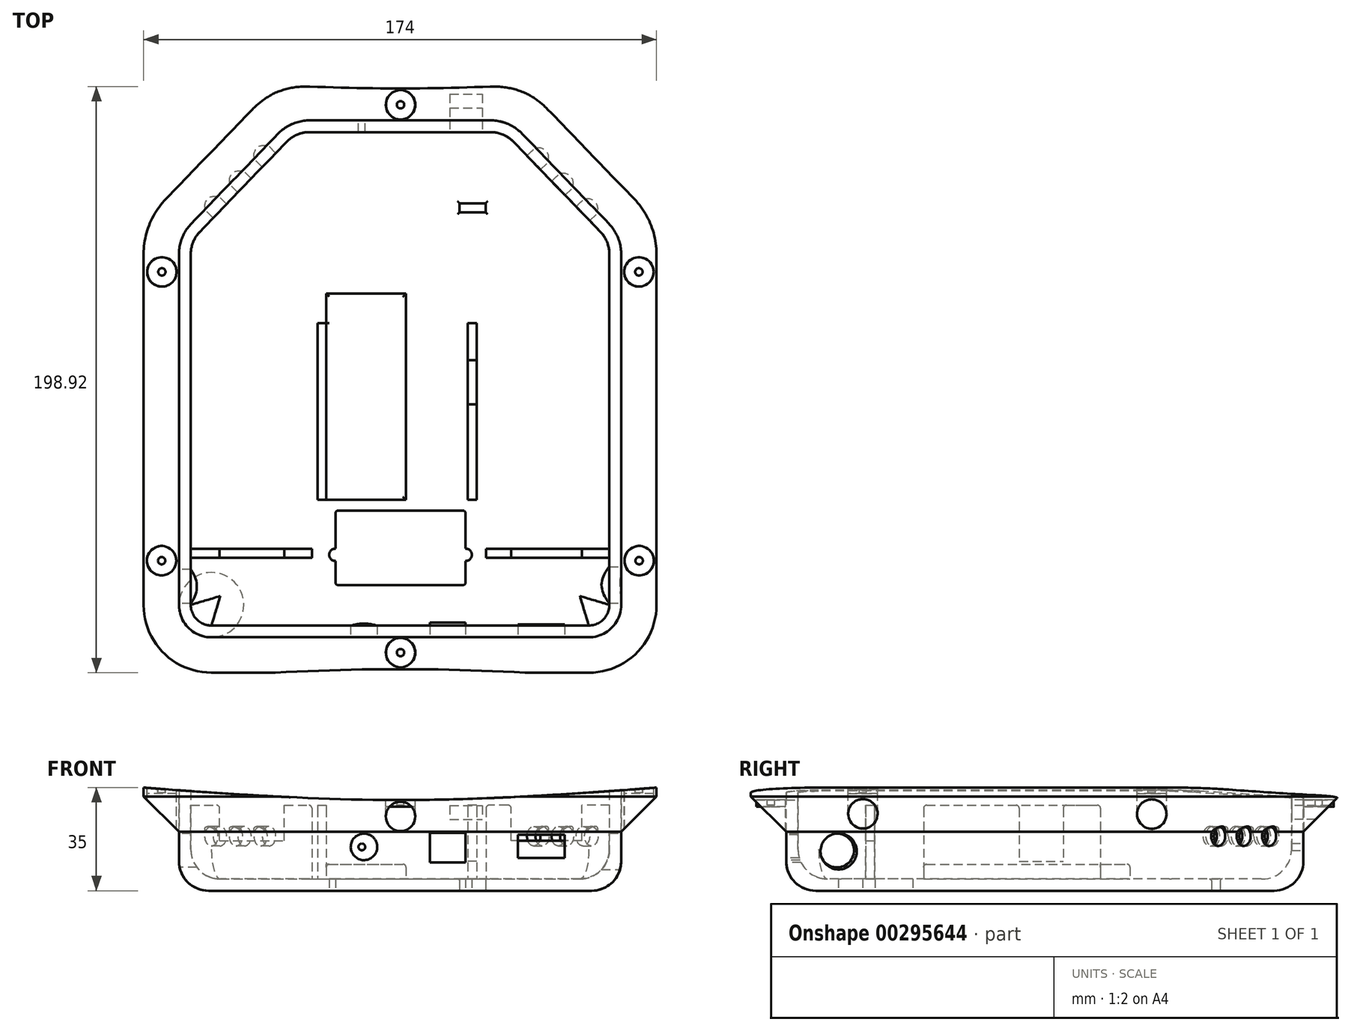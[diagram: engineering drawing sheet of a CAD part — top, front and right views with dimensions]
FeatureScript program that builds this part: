
annotation { "Feature Type Name" : "Feature", "Feature Type Description" : "" }
export const myFeature = defineFeature(function(context is Context, id is Id, definition is map)
    precondition{}
    {
        {
            var Q0;
            Q0=qCreatedBy(makeId("Top.planeOp"),FACE);
            var sketch = newSketch(context, id + "F0", { "sketchPlane" : qUnion([Q0])});
            skLineSegment(sketch, "E0.top", {"start": v(-64.15, -84.77) * mm, "end": v(63.85, -84.77) * mm});
            skLineSegment(sketch, "E0.left", {"start": v(-75.15, 45.23) * mm, "end": v(-75.15, -73.77) * mm});
            skLineSegment(sketch, "E0.right", {"start": v(74.85, 45.23) * mm, "end": v(74.85, -73.77) * mm});
            skLineSegment(sketch, "E1", {"start": v(-41.58, 86.08) * mm, "end": v(-70.95, 55.65) * mm});
            skLineSegment(sketch, "E2", {"start": v(41.27, 86.08) * mm, "end": v(70.64, 55.65) * mm});
            skLineSegment(sketch, "E3", {"start": v(-30.78, 90.67) * mm, "end": v(30.48, 90.67) * mm});
            skPoint(sketch, "E4.visualSharp", {"position": v(-37.15, 90.67) * mm});
            skArc(sketch, "E4.filletArc", {"start": v(-30.78, 90.67) * mm, "mid": v(-36.65, 89.47) * mm, "end": v(-41.58, 86.08) * mm});
            skPoint(sketch, "E5.newPointA", {"position": v(-76.04, 50.37) * mm});
            skArc(sketch, "E5.filletArc", {"start": v(-70.95, 55.65) * mm, "mid": v(-74.06, 50.85) * mm, "end": v(-75.15, 45.23) * mm});
            skPoint(sketch, "E6.newPointA", {"position": v(75.73, 50.37) * mm});
            skArc(sketch, "E6.filletArc", {"start": v(74.85, 45.23) * mm, "mid": v(73.75, 50.85) * mm, "end": v(70.64, 55.65) * mm});
            skPoint(sketch, "E7.visualSharp", {"position": v(36.85, 90.67) * mm});
            skArc(sketch, "E7.filletArc", {"start": v(41.27, 86.08) * mm, "mid": v(36.34, 89.47) * mm, "end": v(30.48, 90.67) * mm});
            skPoint(sketch, "E8.visualSharp", {"position": v(74.85, -84.77) * mm});
            skArc(sketch, "E8.filletArc", {"start": v(63.85, -84.77) * mm, "mid": v(71.62, -81.55) * mm, "end": v(74.85, -73.77) * mm});
            skPoint(sketch, "E9.visualSharp", {"position": v(-75.15, -84.77) * mm});
            skArc(sketch, "E9.filletArc", {"start": v(-75.15, -73.77) * mm, "mid": v(-71.93, -81.55) * mm, "end": v(-64.15, -84.77) * mm});
            skSolve(sketch);
        }
        {
            var Q0;
            Q0=qSketchRegion(id+"F0",true);
            extrude(context, id + "F1", {"entities" : qUnion([Q0]), "depth" : 35 * mm, "offsetDistance" : 25 * mm});
        }
        {
            var Q0;
            Q0=makeQuery(id+"F1.opExtrude","CAP_FACE",FACE,{"disambiguationData":[OSD([sQuery(id+"F0.wireOp",EDGE,"E0.bottom"),sQuery(id+"F0.wireOp",EDGE,"E0.top"),sQuery(id+"F0.wireOp",EDGE,"E0.left"),sQuery(id+"F0.wireOp",EDGE,"E0.right")])],"isStart":false});
            shell(context, id + "F2", {"entities" : qUnion([Q0]), "thickness" : 4 * mm});
        }
        {
            var Q0;
            {var subQ0=sQuery(id+"F0.wireOp",EDGE,"E0.left");Q0=makeQuery(id+"F2.opShell","OFFSET_EDGE",EDGE,{"disambiguationData":[OSD([subQ0]),TDD([makeQuery(id+"F1.opExtrude","CAP_EDGE",EDGE,{"disambiguationData":[OSD([subQ0])],"isStart":true})])]});}
            var Q1;
            {var subQ0=sQuery(id+"F0.wireOp",EDGE,"E0.right");Q1=makeQuery(id+"F2.opShell","OFFSET_EDGE",EDGE,{"disambiguationData":[OSD([subQ0]),TDD([makeQuery(id+"F1.opExtrude","CAP_EDGE",EDGE,{"disambiguationData":[OSD([subQ0])],"isStart":true})])]});}
            var Q2;
            {var subQ0=sQuery(id+"F0.wireOp",EDGE,"E0.bottom");Q2=makeQuery(id+"F2.opShell","OFFSET_EDGE",EDGE,{"disambiguationData":[OSD([subQ0]),TDD([makeQuery(id+"F1.opExtrude","CAP_EDGE",EDGE,{"disambiguationData":[OSD([subQ0])],"isStart":true})])]});}
            var Q3;
            {var subQ0=sQuery(id+"F0.wireOp",EDGE,"eb44f88f-92e2-455c-a940-064eeaeaa6cd.filletArc");Q3=makeQuery(id+"F2.opShell","OFFSET_EDGE",EDGE,{"disambiguationData":[OSD([subQ0]),TDD([makeQuery(id+"F1.opExtrude","CAP_EDGE",EDGE,{"disambiguationData":[OSD([subQ0])],"isStart":true})])]});}
            var Q4;
            {var subQ0=sQuery(id+"F0.wireOp",EDGE,"d43988df-4d56-44c7-8095-11d52762e103.filletArc");Q4=makeQuery(id+"F2.opShell","OFFSET_EDGE",EDGE,{"disambiguationData":[OSD([subQ0]),TDD([makeQuery(id+"F1.opExtrude","CAP_EDGE",EDGE,{"disambiguationData":[OSD([subQ0])],"isStart":true})])]});}
            fillet(context, id + "F3", {"entities" : qUnion([Q0, Q1, Q2, Q3, Q4]), "radius" : 10 * mm, "tangentPropagation" : true, "allowEdgeOverflow" : false});
        }
        {
            var Q0;
            Q0=makeQuery(id+"F1.opExtrude","CAP_EDGE",EDGE,{"disambiguationData":[OSD([sQuery(id+"F0.wireOp",EDGE,"E0.right")])],"isStart":true});
            var Q1;
            Q1=makeQuery(id+"F1.opExtrude","CAP_EDGE",EDGE,{"disambiguationData":[OSD([sQuery(id+"F0.wireOp",EDGE,"d43988df-4d56-44c7-8095-11d52762e103.filletArc")])],"isStart":true});
            var Q2;
            Q2=makeQuery(id+"F1.opExtrude","CAP_EDGE",EDGE,{"disambiguationData":[OSD([sQuery(id+"F0.wireOp",EDGE,"E0.bottom")])],"isStart":true});
            var Q3;
            Q3=makeQuery(id+"F1.opExtrude","CAP_EDGE",EDGE,{"disambiguationData":[OSD([sQuery(id+"F0.wireOp",EDGE,"E0.left")])],"isStart":true});
            var Q4;
            Q4=makeQuery(id+"F1.opExtrude","CAP_EDGE",EDGE,{"disambiguationData":[OSD([sQuery(id+"F0.wireOp",EDGE,"eb44f88f-92e2-455c-a940-064eeaeaa6cd.filletArc")])],"isStart":true});
            fillet(context, id + "F4", {"entities" : qUnion([Q0, Q1, Q2, Q3, Q4]), "radius" : 10 * mm, "tangentPropagation" : true, "allowEdgeOverflow" : false});
        }
        {
            var Q0;
            Q0=makeQuery(id+"FrwUbtnxUC9HyyJ_1.boolean.opBoolean","MERGE",FACE,{"derivedFrom":[makeQuery(id+"F1.opExtrude","CAP_FACE",FACE,{"disambiguationData":[OSD([sQuery(id+"F0.wireOp",EDGE,"E0.bottom"),sQuery(id+"F0.wireOp",EDGE,"E0.top"),sQuery(id+"F0.wireOp",EDGE,"E0.left"),sQuery(id+"F0.wireOp",EDGE,"E0.right"),sQuery(id+"F0.wireOp",EDGE,"eb44f88f-92e2-455c-a940-064eeaeaa6cd.filletArc"),sQuery(id+"F0.wireOp",EDGE,"d43988df-4d56-44c7-8095-11d52762e103.filletArc")])],"isStart":false}),makeQuery(id+"FrwUbtnxUC9HyyJ_1.opExtrude","CAP_FACE",FACE,{"disambiguationData":[OSD([sQuery(id+"FibHU4dr98Ndzw2_1.wireOp",EDGE,"9rjzK8EU-co4c-AKP1-GJnL-XDDrkJgZbtAS.bottom"),sQuery(id+"FibHU4dr98Ndzw2_1.wireOp",EDGE,"9rjzK8EU-co4c-AKP1-GJnL-XDDrkJgZbtAS.top"),sQuery(id+"FibHU4dr98Ndzw2_1.wireOp",EDGE,"9rjzK8EU-co4c-AKP1-GJnL-XDDrkJgZbtAS.left"),sQuery(id+"FibHU4dr98Ndzw2_1.wireOp",EDGE,"9rjzK8EU-co4c-AKP1-GJnL-XDDrkJgZbtAS.right")])],"isStart":true})]});
            var sketch = newSketch(context, id + "F5", { "sketchPlane" : qUnion([Q0])});
            skLineSegment(sketch, "E10", {"start": v(-30.78, 90.67) * mm, "end": v(30.48, 90.67) * mm});
            skLineSegment(sketch, "E11", {"start": v(74.85, 45.23) * mm, "end": v(74.85, -73.77) * mm});
            skLineSegment(sketch, "E12", {"start": v(-64.15, -84.77) * mm, "end": v(63.85, -84.77) * mm});
            skLineSegment(sketch, "E13", {"start": v(-75.15, -73.77) * mm, "end": v(-75.15, 45.23) * mm});
            skLineSegment(sketch, "E14", {"start": v(-41.58, 86.08) * mm, "end": v(-70.95, 55.65) * mm});
            skLineSegment(sketch, "E15", {"start": v(41.27, 86.08) * mm, "end": v(70.64, 55.65) * mm});
            skPoint(sketch, "E16.newPointB", {"position": v(-45.04, 90.67) * mm});
            skArc(sketch, "E16.filletArc", {"start": v(-30.78, 90.67) * mm, "mid": v(-36.65, 89.47) * mm, "end": v(-41.58, 86.08) * mm});
            skArc(sketch, "E17.filletArc", {"start": v(41.27, 86.08) * mm, "mid": v(36.34, 89.47) * mm, "end": v(30.48, 90.67) * mm});
            skPoint(sketch, "E18.newPointA", {"position": v(74.85, 61.4) * mm});
            skArc(sketch, "E18.filletArc", {"start": v(74.85, 45.23) * mm, "mid": v(73.75, 50.85) * mm, "end": v(70.64, 55.65) * mm});
            skArc(sketch, "E19.filletArc", {"start": v(-70.95, 55.65) * mm, "mid": v(-74.06, 50.85) * mm, "end": v(-75.15, 45.23) * mm});
            skPoint(sketch, "E20.newPointA", {"position": v(-75.15, -93.2) * mm});
            skPoint(sketch, "E20.newPointB", {"position": v(-86.24, -84.77) * mm});
            skArc(sketch, "E20.filletArc", {"start": v(-75.15, -73.77) * mm, "mid": v(-71.93, -81.55) * mm, "end": v(-64.15, -84.77) * mm});
            skArc(sketch, "E21.filletArc", {"start": v(63.85, -84.77) * mm, "mid": v(71.62, -81.55) * mm, "end": v(74.85, -73.77) * mm});
            skArc(sketch, "E22.0", {"start": v(-87.15, -73.77) * mm, "mid": v(-80.42, -90.03) * mm, "end": v(-64.15, -96.77) * mm});
            skLineSegment(sketch, "E22.1", {"start": v(-30.78, 102.67) * mm, "end": v(30.48, 102.67) * mm});
            skArc(sketch, "E22.2", {"start": v(-30.78, 102.67) * mm, "mid": v(-41.34, 100.52) * mm, "end": v(-50.21, 94.42) * mm});
            skLineSegment(sketch, "E22.3", {"start": v(-50.21, 94.42) * mm, "end": v(-79.58, 63.98) * mm});
            skArc(sketch, "E22.4", {"start": v(-79.58, 63.98) * mm, "mid": v(-85.19, 55.34) * mm, "end": v(-87.15, 45.23) * mm});
            skArc(sketch, "E22.5", {"start": v(49.9, 94.42) * mm, "mid": v(41.03, 100.52) * mm, "end": v(30.48, 102.67) * mm});
            skLineSegment(sketch, "E22.6", {"start": v(-87.15, -73.77) * mm, "end": v(-87.15, 45.23) * mm});
            skLineSegment(sketch, "E22.7", {"start": v(49.9, 94.42) * mm, "end": v(79.28, 63.98) * mm});
            skArc(sketch, "E22.8", {"start": v(86.85, 45.23) * mm, "mid": v(84.88, 55.34) * mm, "end": v(79.28, 63.98) * mm});
            skLineSegment(sketch, "E22.9", {"start": v(86.85, 45.23) * mm, "end": v(86.85, -73.77) * mm});
            skArc(sketch, "E22.10", {"start": v(63.85, -96.77) * mm, "mid": v(80.1, -90.03) * mm, "end": v(86.85, -73.77) * mm});
            skLineSegment(sketch, "E22.11", {"start": v(-64.15, -96.77) * mm, "end": v(63.85, -96.77) * mm});
            skSolve(sketch);
        }
        {
            var Q0;
            Q0=qSketchRegion(id+"F5",true);
            extrude(context, id + "F6", {"entities" : qUnion([Q0]), "oppositeDirection" : true, "depth" : 15 * mm});
        }
        {
            var Q0;
            Q0=makeQuery(id+"F6.opExtrude","CAP_EDGE",EDGE,{"disambiguationData":[OSD([sQuery(id+"F5.wireOp",EDGE,"E22.1")])],"isStart":false});
            var Q1;
            Q1=makeQuery(id+"F6.opExtrude","CAP_EDGE",EDGE,{"disambiguationData":[OSD([sQuery(id+"F5.wireOp",EDGE,"E22.2")])],"isStart":false});
            var Q2;
            Q2=makeQuery(id+"F6.opExtrude","CAP_EDGE",EDGE,{"disambiguationData":[OSD([sQuery(id+"F5.wireOp",EDGE,"E22.3")])],"isStart":false});
            var Q3;
            Q3=makeQuery(id+"F6.opExtrude","CAP_EDGE",EDGE,{"disambiguationData":[OSD([sQuery(id+"F5.wireOp",EDGE,"E22.4")])],"isStart":false});
            var Q4;
            Q4=makeQuery(id+"F6.opExtrude","CAP_EDGE",EDGE,{"disambiguationData":[OSD([sQuery(id+"F5.wireOp",EDGE,"E22.6")])],"isStart":false});
            var Q5;
            Q5=makeQuery(id+"F6.opExtrude","CAP_EDGE",EDGE,{"disambiguationData":[OSD([sQuery(id+"F5.wireOp",EDGE,"E22.0")])],"isStart":false});
            var Q6;
            Q6=makeQuery(id+"F6.opExtrude","CAP_EDGE",EDGE,{"disambiguationData":[OSD([sQuery(id+"F5.wireOp",EDGE,"E22.11")])],"isStart":false});
            var Q7;
            Q7=makeQuery(id+"F6.opExtrude","CAP_EDGE",EDGE,{"disambiguationData":[OSD([sQuery(id+"F5.wireOp",EDGE,"E22.10")])],"isStart":false});
            var Q8;
            Q8=makeQuery(id+"F6.opExtrude","CAP_EDGE",EDGE,{"disambiguationData":[OSD([sQuery(id+"F5.wireOp",EDGE,"E22.9")])],"isStart":false});
            var Q9;
            Q9=makeQuery(id+"F6.opExtrude","CAP_EDGE",EDGE,{"disambiguationData":[OSD([sQuery(id+"F5.wireOp",EDGE,"E22.8")])],"isStart":false});
            var Q10;
            Q10=makeQuery(id+"F6.opExtrude","CAP_EDGE",EDGE,{"disambiguationData":[OSD([sQuery(id+"F5.wireOp",EDGE,"E22.7")])],"isStart":false});
            var Q11;
            Q11=makeQuery(id+"F6.opExtrude","CAP_EDGE",EDGE,{"disambiguationData":[OSD([sQuery(id+"F5.wireOp",EDGE,"E22.5")])],"isStart":false});
            chamfer(context, id + "F7", {"entities" : qUnion([Q0, Q1, Q2, Q3, Q4, Q5, Q6, Q7, Q8, Q9, Q10, Q11]), "width" : 12 * mm, "tangentPropagation" : true});
        }
        {
            var Q0;
            Q0=makeQuery(id+"F6.opExtrude","CAP_FACE",FACE,{"disambiguationData":[OSD([sQuery(id+"F5.wireOp",EDGE,"E10"),sQuery(id+"F5.wireOp",EDGE,"E11"),sQuery(id+"F5.wireOp",EDGE,"E12"),sQuery(id+"F5.wireOp",EDGE,"E13"),sQuery(id+"F5.wireOp",EDGE,"E14"),sQuery(id+"F5.wireOp",EDGE,"E15"),sQuery(id+"F5.wireOp",EDGE,"E16.filletArc"),sQuery(id+"F5.wireOp",EDGE,"E17.filletArc"),sQuery(id+"F5.wireOp",EDGE,"E18.filletArc"),sQuery(id+"F5.wireOp",EDGE,"E19.filletArc"),sQuery(id+"F5.wireOp",EDGE,"E20.filletArc"),sQuery(id+"F5.wireOp",EDGE,"E21.filletArc"),sQuery(id+"F5.wireOp",EDGE,"E22.0"),sQuery(id+"F5.wireOp",EDGE,"E22.1"),sQuery(id+"F5.wireOp",EDGE,"E22.2"),sQuery(id+"F5.wireOp",EDGE,"E22.3"),sQuery(id+"F5.wireOp",EDGE,"E22.4"),sQuery(id+"F5.wireOp",EDGE,"E22.5"),sQuery(id+"F5.wireOp",EDGE,"E22.6"),sQuery(id+"F5.wireOp",EDGE,"E22.7"),sQuery(id+"F5.wireOp",EDGE,"E22.8"),sQuery(id+"F5.wireOp",EDGE,"E22.9"),sQuery(id+"F5.wireOp",EDGE,"E22.10"),sQuery(id+"F5.wireOp",EDGE,"E22.11")])],"isStart":true});
            var sketch = newSketch(context, id + "F8", { "sketchPlane" : qUnion([Q0])});
            skCircle(sketch, "E23", {"center": v(-80.96, 39.23) * mm, "radius": 5 * mm});
            skCircle(sketch, "E24", {"center": v(80.86, 39.23) * mm, "radius": 5 * mm});
            skCircle(sketch, "E25", {"center": v(80.95, -58.77) * mm, "radius": 5 * mm});
            skCircle(sketch, "E26", {"center": v(-81.06, -58.77) * mm, "radius": 5 * mm});
            skSolve(sketch);
        }
        {
            var Q0;
            Q0 = qSketchRegion(id + "F8", true);
            extrude(context, id + "F9", {"entities" : qUnion([Q0]), "operationType" : NewBodyOperationType.REMOVE, "oppositeDirection" : true, "depth" : 15 * mm});
        }
        {
            var Q0;
            Q0=makeQuery(id+"F6.opExtrude","CAP_FACE",FACE,{"disambiguationData":[OSD([sQuery(id+"F5.wireOp",EDGE,"E10"),sQuery(id+"F5.wireOp",EDGE,"E11"),sQuery(id+"F5.wireOp",EDGE,"E12"),sQuery(id+"F5.wireOp",EDGE,"E13"),sQuery(id+"F5.wireOp",EDGE,"E14"),sQuery(id+"F5.wireOp",EDGE,"E15"),sQuery(id+"F5.wireOp",EDGE,"E16.filletArc"),sQuery(id+"F5.wireOp",EDGE,"E17.filletArc"),sQuery(id+"F5.wireOp",EDGE,"E18.filletArc"),sQuery(id+"F5.wireOp",EDGE,"E19.filletArc"),sQuery(id+"F5.wireOp",EDGE,"E20.filletArc"),sQuery(id+"F5.wireOp",EDGE,"E21.filletArc"),sQuery(id+"F5.wireOp",EDGE,"E22.0"),sQuery(id+"F5.wireOp",EDGE,"E22.1"),sQuery(id+"F5.wireOp",EDGE,"E22.2"),sQuery(id+"F5.wireOp",EDGE,"E22.3"),sQuery(id+"F5.wireOp",EDGE,"E22.4"),sQuery(id+"F5.wireOp",EDGE,"E22.5"),sQuery(id+"F5.wireOp",EDGE,"E22.6"),sQuery(id+"F5.wireOp",EDGE,"E22.7"),sQuery(id+"F5.wireOp",EDGE,"E22.8"),sQuery(id+"F5.wireOp",EDGE,"E22.9"),sQuery(id+"F5.wireOp",EDGE,"E22.10"),sQuery(id+"F5.wireOp",EDGE,"E22.11")])],"isStart":true});
            var sketch = newSketch(context, id + "F10", { "sketchPlane" : qUnion([Q0])});
            skCircle(sketch, "E27", {"center": v(-80.96, 39.23) * mm, "radius": 5 * mm});
            skCircle(sketch, "E28", {"center": v(80.86, 39.23) * mm, "radius": 5 * mm});
            skCircle(sketch, "E29", {"center": v(80.95, -58.77) * mm, "radius": 5 * mm});
            skCircle(sketch, "E30", {"center": v(-81.06, -58.77) * mm, "radius": 5 * mm});
            skSolve(sketch);
        }
        {
            var Q0;
            Q0 = qSketchRegion(id + "F10", true);
            extrude(context, id + "F11", {"entities" : qUnion([Q0]), "oppositeDirection" : true, "depth" : 2 * mm});
        }
        {
            var Q0;
            Q0=makeQuery(id+"F11.opExtrude","CAP_FACE",FACE,{"disambiguationData":[OSD([sQuery(id+"F10.wireOp",EDGE,"E27")])],"isStart":true});
            var sketch = newSketch(context, id + "F12", { "sketchPlane" : qUnion([Q0])});
            skCircle(sketch, "E31", {"center": v(-80.96, 39.23) * mm, "radius": 1.25 * mm});
            skSolve(sketch);
        }
        {
            var Q0;
            Q0 = qSketchRegion(id + "F12", true);
            extrude(context, id + "F13", {"entities" : qUnion([Q0]), "operationType" : NewBodyOperationType.REMOVE, "oppositeDirection" : true, "depth" : 1.8 * mm});
        }
        {
            var Q0;
            Q0=makeQuery(id+"F11.opExtrude","CAP_FACE",FACE,{"disambiguationData":[OSD([sQuery(id+"F10.wireOp",EDGE,"E30")])],"isStart":true});
            var sketch = newSketch(context, id + "F14", { "sketchPlane" : qUnion([Q0])});
            skCircle(sketch, "E32", {"center": v(-81.06, -58.77) * mm, "radius": 1.25 * mm});
            skSolve(sketch);
        }
        {
            var Q0;
            Q0 = qSketchRegion(id + "F14", true);
            extrude(context, id + "F15", {"entities" : qUnion([Q0]), "operationType" : NewBodyOperationType.REMOVE, "oppositeDirection" : true, "depth" : 1.8 * mm});
        }
        {
            var Q0;
            Q0=makeQuery(id+"F11.opExtrude","CAP_FACE",FACE,{"disambiguationData":[OSD([sQuery(id+"F10.wireOp",EDGE,"E29")])],"isStart":true});
            var sketch = newSketch(context, id + "F16", { "sketchPlane" : qUnion([Q0])});
            skCircle(sketch, "E33", {"center": v(80.95, -58.77) * mm, "radius": 1.25 * mm});
            skSolve(sketch);
        }
        {
            var Q0;
            Q0 = qSketchRegion(id + "F16", true);
            extrude(context, id + "F17", {"entities" : qUnion([Q0]), "operationType" : NewBodyOperationType.REMOVE, "oppositeDirection" : true, "depth" : 1.8 * mm});
        }
        {
            var Q0;
            Q0=makeQuery(id+"F11.opExtrude","CAP_FACE",FACE,{"disambiguationData":[OSD([sQuery(id+"F10.wireOp",EDGE,"E28")])],"isStart":true});
            var sketch = newSketch(context, id + "F18", { "sketchPlane" : qUnion([Q0])});
            skCircle(sketch, "E34", {"center": v(80.86, 39.23) * mm, "radius": 1.25 * mm});
            skSolve(sketch);
        }
        {
            var Q0;
            Q0 = qSketchRegion(id + "F18", true);
            extrude(context, id + "F19", {"entities" : qUnion([Q0]), "operationType" : NewBodyOperationType.REMOVE, "oppositeDirection" : true, "depth" : 1.8 * mm});
        }
        {
            var Q0;
            Q0=makeQuery(id+"F6.opExtrude","CAP_FACE",FACE,{"disambiguationData":[OSD([sQuery(id+"F5.wireOp",EDGE,"E10"),sQuery(id+"F5.wireOp",EDGE,"E11"),sQuery(id+"F5.wireOp",EDGE,"E12"),sQuery(id+"F5.wireOp",EDGE,"E13"),sQuery(id+"F5.wireOp",EDGE,"E14"),sQuery(id+"F5.wireOp",EDGE,"E15"),sQuery(id+"F5.wireOp",EDGE,"E16.filletArc"),sQuery(id+"F5.wireOp",EDGE,"E17.filletArc"),sQuery(id+"F5.wireOp",EDGE,"E18.filletArc"),sQuery(id+"F5.wireOp",EDGE,"E19.filletArc"),sQuery(id+"F5.wireOp",EDGE,"E20.filletArc"),sQuery(id+"F5.wireOp",EDGE,"E21.filletArc"),sQuery(id+"F5.wireOp",EDGE,"E22.0"),sQuery(id+"F5.wireOp",EDGE,"E22.1"),sQuery(id+"F5.wireOp",EDGE,"E22.2"),sQuery(id+"F5.wireOp",EDGE,"E22.3"),sQuery(id+"F5.wireOp",EDGE,"E22.4"),sQuery(id+"F5.wireOp",EDGE,"E22.5"),sQuery(id+"F5.wireOp",EDGE,"E22.6"),sQuery(id+"F5.wireOp",EDGE,"E22.7"),sQuery(id+"F5.wireOp",EDGE,"E22.8"),sQuery(id+"F5.wireOp",EDGE,"E22.9"),sQuery(id+"F5.wireOp",EDGE,"E22.10"),sQuery(id+"F5.wireOp",EDGE,"E22.11")])],"isStart":true});
            var sketch = newSketch(context, id + "F20", { "sketchPlane" : qUnion([Q0])});
            skCircle(sketch, "E35", {"center": v(0, -89.96) * mm, "radius": 5 * mm});
            skCircle(sketch, "E36", {"center": v(0, 95.93) * mm, "radius": 5 * mm});
            skSolve(sketch);
        }
        {
            var Q0;
            Q0 = qSketchRegion(id + "F20", true);
            extrude(context, id + "F21", {"entities" : qUnion([Q0]), "operationType" : NewBodyOperationType.REMOVE, "oppositeDirection" : true, "depth" : 15 * mm});
        }
        {
            var Q0;
            Q0=makeQuery(id+"F6.opExtrude","CAP_FACE",FACE,{"disambiguationData":[OSD([sQuery(id+"F5.wireOp",EDGE,"E10"),sQuery(id+"F5.wireOp",EDGE,"E11"),sQuery(id+"F5.wireOp",EDGE,"E12"),sQuery(id+"F5.wireOp",EDGE,"E13"),sQuery(id+"F5.wireOp",EDGE,"E14"),sQuery(id+"F5.wireOp",EDGE,"E15"),sQuery(id+"F5.wireOp",EDGE,"E16.filletArc"),sQuery(id+"F5.wireOp",EDGE,"E17.filletArc"),sQuery(id+"F5.wireOp",EDGE,"E18.filletArc"),sQuery(id+"F5.wireOp",EDGE,"E19.filletArc"),sQuery(id+"F5.wireOp",EDGE,"E20.filletArc"),sQuery(id+"F5.wireOp",EDGE,"E21.filletArc"),sQuery(id+"F5.wireOp",EDGE,"E22.0"),sQuery(id+"F5.wireOp",EDGE,"E22.1"),sQuery(id+"F5.wireOp",EDGE,"E22.2"),sQuery(id+"F5.wireOp",EDGE,"E22.3"),sQuery(id+"F5.wireOp",EDGE,"E22.4"),sQuery(id+"F5.wireOp",EDGE,"E22.5"),sQuery(id+"F5.wireOp",EDGE,"E22.6"),sQuery(id+"F5.wireOp",EDGE,"E22.7"),sQuery(id+"F5.wireOp",EDGE,"E22.8"),sQuery(id+"F5.wireOp",EDGE,"E22.9"),sQuery(id+"F5.wireOp",EDGE,"E22.10"),sQuery(id+"F5.wireOp",EDGE,"E22.11")])],"isStart":true});
            var sketch = newSketch(context, id + "F22", { "sketchPlane" : qUnion([Q0])});
            skCircle(sketch, "E37", {"center": v(0, -89.96) * mm, "radius": 5 * mm});
            skCircle(sketch, "E38", {"center": v(0, 95.93) * mm, "radius": 5 * mm});
            skSolve(sketch);
        }
        {
            var Q0;
            Q0 = qSketchRegion(id + "F22", true);
            extrude(context, id + "F23", {"entities" : qUnion([Q0]), "oppositeDirection" : true, "depth" : 6.5 * mm, "offsetDistance" : 25 * mm});
        }
        {
            var Q0;
            Q0=makeQuery(id+"F23.opExtrude","CAP_FACE",FACE,{"disambiguationData":[OSD([sQuery(id+"F22.wireOp",EDGE,"E38")])],"isStart":true});
            var sketch = newSketch(context, id + "F24", { "sketchPlane" : qUnion([Q0])});
            skCircle(sketch, "E39", {"center": v(0, 95.93) * mm, "radius": 1.25 * mm});
            skSolve(sketch);
        }
        {
            var Q0;
            Q0 = qSketchRegion(id + "F24", true);
            extrude(context, id + "F25", {"entities" : qUnion([Q0]), "operationType" : NewBodyOperationType.REMOVE, "oppositeDirection" : true, "depth" : 6.3 * mm, "offsetDistance" : 25 * mm});
        }
        {
            var Q0;
            Q0=makeQuery(id+"F23.opExtrude","CAP_FACE",FACE,{"disambiguationData":[OSD([sQuery(id+"F22.wireOp",EDGE,"E37")])],"isStart":true});
            var sketch = newSketch(context, id + "F26", { "sketchPlane" : qUnion([Q0])});
            skCircle(sketch, "E40", {"center": v(0, -89.96) * mm, "radius": 1.25 * mm});
            skSolve(sketch);
        }
        {
            var Q0;
            Q0 = qSketchRegion(id + "F26", true);
            extrude(context, id + "F27", {"entities" : qUnion([Q0]), "operationType" : NewBodyOperationType.REMOVE, "oppositeDirection" : true, "depth" : 6 * mm});
        }
        {
            var Q0;
            Q0=makeQuery(id+"F6.opExtrude","SWEPT_FACE",FACE,{"disambiguationData":[OSD([sQuery(id+"F5.wireOp",EDGE,"E22.11")])]});
            var sketch = newSketch(context, id + "F28", { "sketchPlane" : qUnion([Q0])});
            skFitSpline(sketch, "E41", {"points": [v(-87.15, 35) * mm, v(-0.13, 30.8) * mm, v(86.85, 35) * mm], "startDerivative": vector(174.23, -13.41) * mm, "endDerivative": vector(173.77, 13.42) * mm});
            skLineSegment(sketch, "E42", {"start": v(86.85, 35) * mm, "end": v(-87.15, 35) * mm});
            skSolve(sketch);
        }
        {
            var Q0;
            Q0 = qSketchRegion(id + "F28", true);
            extrude(context, id + "F29", {"entities" : qUnion([Q0]), "operationType" : NewBodyOperationType.REMOVE, "oppositeDirection" : true, "depth" : 200 * mm});
        }
        {
            var Q0;
            Q0=makeQuery(id+"F2.opShell","OFFSET_FACE",FACE,{"disambiguationData":[OSD([sQuery(id+"F0.wireOp",EDGE,"E3")])]});
            var sketch = newSketch(context, id + "F30", { "sketchPlane" : qUnion([Q0])});
            skLineSegment(sketch, "E43.bottom", {"start": v(16.7, 28.85) * mm, "end": v(27.7, 28.85) * mm});
            skLineSegment(sketch, "E43.top", {"start": v(16.7, 24.15) * mm, "end": v(27.7, 24.15) * mm});
            skLineSegment(sketch, "E43.left", {"start": v(16.7, 28.85) * mm, "end": v(16.7, 24.15) * mm});
            skLineSegment(sketch, "E43.right", {"start": v(27.7, 28.85) * mm, "end": v(27.7, 24.15) * mm});
            skSolve(sketch);
        }
        {
            var Q0;
            Q0 = qSketchRegion(id + "F30", true);
            extrude(context, id + "F31", {"entities" : qUnion([Q0]), "operationType" : NewBodyOperationType.REMOVE, "oppositeDirection" : true, "depth" : 18 * mm});
        }
        {
            var Q0;
            Q0=makeQuery(id+"F1.opExtrude","SWEPT_FACE",FACE,{"disambiguationData":[OSD([sQuery(id+"F0.wireOp",EDGE,"E0.right")])]});
            var sketch = newSketch(context, id + "F32", { "sketchPlane" : qUnion([Q0])});
            skCircle(sketch, "E44", {"center": v(-67, 13.36) * mm, "radius": 6.15 * mm});
            skSolve(sketch);
        }
        {
            var Q0;
            Q0 = qSketchRegion(id + "F32", true);
            extrude(context, id + "F33", {"entities" : qUnion([Q0]), "operationType" : NewBodyOperationType.REMOVE, "endBound" : BoundingType.SYMMETRIC, "oppositeDirection" : true, "depth" : 20 * mm});
        }
        {
            var Q0;
            Q0=makeQuery(id+"F1.opExtrude","SWEPT_FACE",FACE,{"disambiguationData":[OSD([sQuery(id+"F0.wireOp",EDGE,"E0.left")])]});
            var sketch = newSketch(context, id + "F34", { "sketchPlane" : qUnion([Q0])});
            skCircle(sketch, "E45", {"center": v(67.54, 13.66) * mm, "radius": 5.75 * mm});
            skSolve(sketch);
        }
        {
            var Q0;
            Q0 = qSketchRegion(id + "F34", true);
            extrude(context, id + "F35", {"entities" : qUnion([Q0]), "operationType" : NewBodyOperationType.REMOVE, "endBound" : BoundingType.SYMMETRIC, "oppositeDirection" : true, "depth" : 20 * mm});
        }
        {
            var Q0;
            Q0=makeQuery(id+"F1.opExtrude","SWEPT_FACE",FACE,{"disambiguationData":[OSD([sQuery(id+"F0.wireOp",EDGE,"E1")])]});
            var sketch = newSketch(context, id + "F36", { "sketchPlane" : qUnion([Q0])});
            skCircle(sketch, "E46", {"center": v(-24.58, 18.5) * mm, "radius": 3.3 * mm});
            skCircle(sketch, "E47", {"center": v(-12.58, 18.5) * mm, "radius": 3.3 * mm});
            skCircle(sketch, "E48", {"center": v(-0.58, 18.5) * mm, "radius": 3.3 * mm});
            skSolve(sketch);
        }
        {
            var Q0;
            Q0=makeQuery(id+"F1.opExtrude","SWEPT_FACE",FACE,{"disambiguationData":[OSD([sQuery(id+"F0.wireOp",EDGE,"E2")])]});
            var sketch = newSketch(context, id + "F37", { "sketchPlane" : qUnion([Q0])});
            skCircle(sketch, "E49", {"center": v(-0.5, 18.5) * mm, "radius": 3.3 * mm});
            skCircle(sketch, "E50", {"center": v(11.5, 18.5) * mm, "radius": 3.3 * mm});
            skCircle(sketch, "E51", {"center": v(23.5, 18.5) * mm, "radius": 3.3 * mm});
            skSolve(sketch);
        }
        {
            var Q0;
            Q0 = qSketchRegion(id + "F36", true);
            extrude(context, id + "F38", {"entities" : qUnion([Q0]), "operationType" : NewBodyOperationType.REMOVE, "endBound" : BoundingType.SYMMETRIC, "oppositeDirection" : true, "depth" : 20 * mm});
        }
        {
            var Q0;
            Q0 = qSketchRegion(id + "F37", true);
            extrude(context, id + "F39", {"entities" : qUnion([Q0]), "operationType" : NewBodyOperationType.REMOVE, "endBound" : BoundingType.SYMMETRIC, "oppositeDirection" : true, "depth" : 20 * mm});
        }
        {
            var Q0;
            Q0=makeQuery(id+"F1.opExtrude","SWEPT_FACE",FACE,{"disambiguationData":[OSD([sQuery(id+"F0.wireOp",EDGE,"E3")])]});
            var sketch = newSketch(context, id + "F40", { "sketchPlane" : qUnion([Q0])});
            skCircle(sketch, "E52", {"center": v(13.13, 14.87) * mm, "radius": 1.15 * mm});
            skSolve(sketch);
        }
        {
            var Q0;
            Q0 = qSketchRegion(id + "F40", true);
            extrude(context, id + "F41", {"entities" : qUnion([Q0]), "operationType" : NewBodyOperationType.REMOVE, "oppositeDirection" : true, "depth" : 5 * mm});
        }
        {
            var Q0;
            Q0=makeQuery(id+"F1.opExtrude","SWEPT_FACE",FACE,{"disambiguationData":[OSD([sQuery(id+"F0.wireOp",EDGE,"E0.top")])]});
            var sketch = newSketch(context, id + "F42", { "sketchPlane" : qUnion([Q0])});
            skLineSegment(sketch, "E53.bottom", {"start": v(55.64, 11.12) * mm, "end": v(39.84, 11.12) * mm});
            skLineSegment(sketch, "E53.top", {"start": v(55.64, 19.02) * mm, "end": v(39.84, 19.02) * mm});
            skLineSegment(sketch, "E53.left", {"start": v(55.64, 11.12) * mm, "end": v(55.64, 19.02) * mm});
            skLineSegment(sketch, "E53.right", {"start": v(39.84, 11.12) * mm, "end": v(39.84, 19.02) * mm});
            skSolve(sketch);
        }
        {
            var Q0;
            Q0 = qSketchRegion(id + "F42", true);
            extrude(context, id + "F43", {"entities" : qUnion([Q0]), "operationType" : NewBodyOperationType.REMOVE, "oppositeDirection" : true, "depth" : 8 * mm});
        }
        {
            var Q0;
            Q0=makeQuery(id+"F1.opExtrude","SWEPT_FACE",FACE,{"disambiguationData":[OSD([sQuery(id+"F0.wireOp",EDGE,"E0.top")])]});
            var sketch = newSketch(context, id + "F44", { "sketchPlane" : qUnion([Q0])});
            skCircle(sketch, "E54", {"center": v(-12.4, 14.88) * mm, "radius": 4.5 * mm});
            skSolve(sketch);
        }
        {
            var Q0;
            Q0 = qSketchRegion(id + "F44", true);
            extrude(context, id + "F45", {"entities" : qUnion([Q0]), "operationType" : NewBodyOperationType.REMOVE, "endBound" : BoundingType.SYMMETRIC, "oppositeDirection" : true, "depth" : 20 * mm});
        }
        {
            var Q0;
            Q0=makeQuery(id+"F1.opExtrude","CAP_FACE",FACE,{"disambiguationData":[OSD([sQuery(id+"F0.wireOp",EDGE,"E0.top"),sQuery(id+"F0.wireOp",EDGE,"E0.left"),sQuery(id+"F0.wireOp",EDGE,"E0.right"),sQuery(id+"F0.wireOp",EDGE,"E1"),sQuery(id+"F0.wireOp",EDGE,"E2"),sQuery(id+"F0.wireOp",EDGE,"E3"),sQuery(id+"F0.wireOp",EDGE,"E4.filletArc"),sQuery(id+"F0.wireOp",EDGE,"E5.filletArc"),sQuery(id+"F0.wireOp",EDGE,"E6.filletArc"),sQuery(id+"F0.wireOp",EDGE,"E7.filletArc"),sQuery(id+"F0.wireOp",EDGE,"E8.filletArc"),sQuery(id+"F0.wireOp",EDGE,"E9.filletArc")])],"isStart":true});
            var sketch = newSketch(context, id + "F46", { "sketchPlane" : qUnion([Q0])});
            skLineSegment(sketch, "E55.bottom", {"start": v(-22.1, 67.07) * mm, "end": v(22.1, 67.07) * mm});
            skLineSegment(sketch, "E55.top", {"start": v(-22.1, 41.77) * mm, "end": v(22.1, 41.77) * mm});
            skLineSegment(sketch, "E55.left", {"start": v(-22.1, 67.07) * mm, "end": v(-22.1, 41.77) * mm});
            skLineSegment(sketch, "E55.right", {"start": v(22.1, 67.07) * mm, "end": v(22.1, 41.77) * mm});
            skSolve(sketch);
        }
        {
            var Q0;
            Q0 = qSketchRegion(id + "F46", true);
            extrude(context, id + "F47", {"entities" : qUnion([Q0]), "operationType" : NewBodyOperationType.REMOVE, "oppositeDirection" : true, "depth" : 5 * mm});
        }
        {
            var Q0;
            Q0=makeQuery(id+"F1.opExtrude","CAP_FACE",FACE,{"disambiguationData":[OSD([sQuery(id+"F0.wireOp",EDGE,"E0.top"),sQuery(id+"F0.wireOp",EDGE,"E0.left"),sQuery(id+"F0.wireOp",EDGE,"E0.right"),sQuery(id+"F0.wireOp",EDGE,"E1"),sQuery(id+"F0.wireOp",EDGE,"E2"),sQuery(id+"F0.wireOp",EDGE,"E3"),sQuery(id+"F0.wireOp",EDGE,"E4.filletArc"),sQuery(id+"F0.wireOp",EDGE,"E5.filletArc"),sQuery(id+"F0.wireOp",EDGE,"E6.filletArc"),sQuery(id+"F0.wireOp",EDGE,"E7.filletArc"),sQuery(id+"F0.wireOp",EDGE,"E8.filletArc"),sQuery(id+"F0.wireOp",EDGE,"E9.filletArc")])],"isStart":true});
            var sketch = newSketch(context, id + "F48", { "sketchPlane" : qUnion([Q0])});
            skCircle(sketch, "E56", {"center": v(-22.1, 56.77) * mm, "radius": 2.1 * mm});
            skCircle(sketch, "E57", {"center": v(22.1, 56.77) * mm, "radius": 2.1 * mm});
            skSolve(sketch);
        }
        {
            var Q0;
            Q0 = qSketchRegion(id + "F48", true);
            extrude(context, id + "F49", {"entities" : qUnion([Q0]), "operationType" : NewBodyOperationType.REMOVE, "oppositeDirection" : true, "depth" : 5 * mm});
        }
        {
            var Q0;
            Q0=makeQuery(id+"F1.opExtrude","SWEPT_FACE",FACE,{"disambiguationData":[OSD([sQuery(id+"F0.wireOp",EDGE,"E0.top")])]});
            var sketch = newSketch(context, id + "F50", { "sketchPlane" : qUnion([Q0])});
            skLineSegment(sketch, "E58.bottom", {"start": v(10.02, 19.6) * mm, "end": v(22.02, 19.6) * mm});
            skLineSegment(sketch, "E58.top", {"start": v(10.02, 9.6) * mm, "end": v(22.02, 9.6) * mm});
            skLineSegment(sketch, "E58.left", {"start": v(10.02, 19.6) * mm, "end": v(10.02, 9.6) * mm});
            skLineSegment(sketch, "E58.right", {"start": v(22.02, 19.6) * mm, "end": v(22.02, 9.6) * mm});
            skPoint(sketch, "E58.middle", {"position": v(16.02, 14.6) * mm});
            skSolve(sketch);
        }
        {
            var Q0;
            Q0 = qSketchRegion(id + "F50", true);
            extrude(context, id + "F51", {"entities" : qUnion([Q0]), "operationType" : NewBodyOperationType.REMOVE, "endBound" : BoundingType.SYMMETRIC, "oppositeDirection" : true, "depth" : 20 * mm});
        }
        {
            var Q0;
            Q0=makeQuery(id+"F47.boolean.opBoolean","COPY",EDGE,{"derivedFrom":makeQuery(id+"F47.opExtrude","SWEPT_EDGE",EDGE,{"disambiguationData":[OSD([sQuery(id+"F46.wireOp",EDGE,"E55.bottom"),sQuery(id+"F46.wireOp",EDGE,"E55.right")])]})});
            var Q1;
            Q1=makeQuery(id+"F47.boolean.opBoolean","COPY",EDGE,{"derivedFrom":makeQuery(id+"F47.opExtrude","SWEPT_EDGE",EDGE,{"disambiguationData":[OSD([sQuery(id+"F46.wireOp",EDGE,"E55.bottom"),sQuery(id+"F46.wireOp",EDGE,"E55.left")])]})});
            var Q2;
            Q2=makeQuery(id+"F47.boolean.opBoolean","COPY",EDGE,{"derivedFrom":makeQuery(id+"F47.opExtrude","SWEPT_EDGE",EDGE,{"disambiguationData":[OSD([sQuery(id+"F46.wireOp",EDGE,"E55.top"),sQuery(id+"F46.wireOp",EDGE,"E55.left")])]})});
            var Q3;
            Q3=makeQuery(id+"F47.boolean.opBoolean","COPY",EDGE,{"derivedFrom":makeQuery(id+"F47.opExtrude","SWEPT_EDGE",EDGE,{"disambiguationData":[OSD([sQuery(id+"F46.wireOp",EDGE,"E55.top"),sQuery(id+"F46.wireOp",EDGE,"E55.right")])]})});
            fillet(context, id + "F52", {"entities" : qUnion([Q0, Q1, Q2, Q3]), "radius" : 1 * mm, "tangentPropagation" : true, "allowEdgeOverflow" : false});
        }
        {
            var Q0;
            Q0=makeQuery(id+"F2.opShell","OFFSET_FACE",FACE,{"disambiguationData":[OSD([sQuery(id+"F0.wireOp",EDGE,"E0.top"),sQuery(id+"F0.wireOp",EDGE,"E0.left"),sQuery(id+"F0.wireOp",EDGE,"E0.right"),sQuery(id+"F0.wireOp",EDGE,"E1"),sQuery(id+"F0.wireOp",EDGE,"E2"),sQuery(id+"F0.wireOp",EDGE,"E3"),sQuery(id+"F0.wireOp",EDGE,"E4.filletArc"),sQuery(id+"F0.wireOp",EDGE,"E5.filletArc"),sQuery(id+"F0.wireOp",EDGE,"E6.filletArc"),sQuery(id+"F0.wireOp",EDGE,"E7.filletArc"),sQuery(id+"F0.wireOp",EDGE,"E8.filletArc"),sQuery(id+"F0.wireOp",EDGE,"E9.filletArc")])]});
            var sketch = newSketch(context, id + "F53", { "sketchPlane" : qUnion([Q0])});
            skLineSegment(sketch, "E59.bottom", {"start": v(-28.15, -38.16) * mm, "end": v(-25.15, -38.16) * mm});
            skLineSegment(sketch, "E59.top", {"start": v(-28.15, 21.84) * mm, "end": v(-25.15, 21.84) * mm});
            skLineSegment(sketch, "E59.left", {"start": v(-28.15, -38.16) * mm, "end": v(-28.15, 21.84) * mm});
            skLineSegment(sketch, "E59.right", {"start": v(-25.15, -38.16) * mm, "end": v(-25.15, 21.84) * mm});
            skLineSegment(sketch, "E60.bottom", {"start": v(25.83, -38.16) * mm, "end": v(22.83, -38.16) * mm});
            skLineSegment(sketch, "E60.top", {"start": v(25.83, -5.77) * mm, "end": v(22.83, -5.77) * mm});
            skLineSegment(sketch, "E60.left", {"start": v(25.83, -38.16) * mm, "end": v(25.83, -5.77) * mm});
            skLineSegment(sketch, "E60.right", {"start": v(22.83, -38.16) * mm, "end": v(22.83, -5.77) * mm});
            skLineSegment(sketch, "E61.bottom", {"start": v(25.83, 9.23) * mm, "end": v(22.83, 9.23) * mm});
            skLineSegment(sketch, "E61.top", {"start": v(25.83, 21.84) * mm, "end": v(22.83, 21.84) * mm});
            skLineSegment(sketch, "E61.left", {"start": v(25.83, 9.23) * mm, "end": v(25.83, 21.84) * mm});
            skLineSegment(sketch, "E61.right", {"start": v(22.83, 9.23) * mm, "end": v(22.83, 21.84) * mm});
            skLineSegment(sketch, "E62.bottom", {"start": v(71.23, -57.77) * mm, "end": v(29.03, -57.77) * mm});
            skLineSegment(sketch, "E62.top", {"start": v(71.23, -54.77) * mm, "end": v(29.03, -54.77) * mm});
            skLineSegment(sketch, "E62.left", {"start": v(71.23, -57.77) * mm, "end": v(71.23, -54.77) * mm});
            skLineSegment(sketch, "E62.right", {"start": v(29.03, -57.77) * mm, "end": v(29.03, -54.77) * mm});
            skLineSegment(sketch, "E63.bottom", {"start": v(-71.65, -57.77) * mm, "end": v(-30.08, -57.77) * mm});
            skLineSegment(sketch, "E63.top", {"start": v(-71.65, -54.77) * mm, "end": v(-30.08, -54.77) * mm});
            skLineSegment(sketch, "E63.left", {"start": v(-71.65, -57.77) * mm, "end": v(-71.65, -54.77) * mm});
            skLineSegment(sketch, "E63.right", {"start": v(-30.08, -57.77) * mm, "end": v(-30.08, -54.77) * mm});
            skSolve(sketch);
        }
        {
            var Q0;
            Q0 = qSketchRegion(id + "F53", true);
            extrude(context, id + "F54", {"entities" : qUnion([Q0]), "operationType" : NewBodyOperationType.ADD, "depth" : 25 * mm});
        }
        {
            var Q0;
            Q0=makeQuery(id+"F2.opShell","OFFSET_FACE",FACE,{"disambiguationData":[OSD([sQuery(id+"F0.wireOp",EDGE,"E0.top"),sQuery(id+"F0.wireOp",EDGE,"E0.left"),sQuery(id+"F0.wireOp",EDGE,"E0.right"),sQuery(id+"F0.wireOp",EDGE,"E1"),sQuery(id+"F0.wireOp",EDGE,"E2"),sQuery(id+"F0.wireOp",EDGE,"E3"),sQuery(id+"F0.wireOp",EDGE,"E4.filletArc"),sQuery(id+"F0.wireOp",EDGE,"E5.filletArc"),sQuery(id+"F0.wireOp",EDGE,"E6.filletArc"),sQuery(id+"F0.wireOp",EDGE,"E7.filletArc"),sQuery(id+"F0.wireOp",EDGE,"E8.filletArc"),sQuery(id+"F0.wireOp",EDGE,"E9.filletArc")])]});
            var sketch = newSketch(context, id + "F55", { "sketchPlane" : qUnion([Q0])});
            skLineSegment(sketch, "E64.bottom", {"start": v(25.83, -5.77) * mm, "end": v(22.83, -5.77) * mm});
            skLineSegment(sketch, "E64.top", {"start": v(25.83, 9.23) * mm, "end": v(22.83, 9.23) * mm});
            skLineSegment(sketch, "E64.left", {"start": v(25.83, -5.77) * mm, "end": v(25.83, 9.23) * mm});
            skLineSegment(sketch, "E64.right", {"start": v(22.83, -5.77) * mm, "end": v(22.83, 9.23) * mm});
            skSolve(sketch);
        }
        {
            var Q0;
            Q0 = qSketchRegion(id + "F55", true);
            extrude(context, id + "F56", {"entities" : qUnion([Q0]), "operationType" : NewBodyOperationType.ADD, "depth" : 6 * mm});
        }
        {
            var Q0;
            Q0=makeQuery(id+"F54.opExtrude","CAP_EDGE",EDGE,{"disambiguationData":[OSD([sQuery(id+"F53.wireOp",EDGE,"E60.bottom")])],"isStart":false});
            var Q1;
            Q1=makeQuery(id+"F54.opExtrude","CAP_EDGE",EDGE,{"disambiguationData":[OSD([sQuery(id+"F53.wireOp",EDGE,"E59.bottom")])],"isStart":false});
            var Q2;
            Q2=makeQuery(id+"F54.opExtrude","CAP_EDGE",EDGE,{"disambiguationData":[OSD([sQuery(id+"F53.wireOp",EDGE,"E61.top")])],"isStart":false});
            var Q3;
            Q3=makeQuery(id+"F54.opExtrude","CAP_EDGE",EDGE,{"disambiguationData":[OSD([sQuery(id+"F53.wireOp",EDGE,"E61.bottom")])],"isStart":false});
            var Q4;
            Q4=makeQuery(id+"F54.opExtrude","CAP_EDGE",EDGE,{"disambiguationData":[OSD([sQuery(id+"F53.wireOp",EDGE,"E60.top")])],"isStart":false});
            var Q5;
            Q5=makeQuery(id+"F54.opExtrude","CAP_EDGE",EDGE,{"disambiguationData":[OSD([sQuery(id+"F53.wireOp",EDGE,"E59.top")])],"isStart":false});
            fillet(context, id + "F57", {"entities" : qUnion([Q0, Q1, Q2, Q3, Q4, Q5]), "radius" : 1 * mm, "tangentPropagation" : true, "allowEdgeOverflow" : false});
        }
        {
            var Q0;
            Q0=makeQuery(id+"F54.opExtrude","CAP_FACE",FACE,{"disambiguationData":[OSD([sQuery(id+"F53.wireOp",EDGE,"E62.bottom"),sQuery(id+"F53.wireOp",EDGE,"E62.top"),sQuery(id+"F53.wireOp",EDGE,"E62.left"),sQuery(id+"F53.wireOp",EDGE,"E62.right")])],"isStart":false});
            var sketch = newSketch(context, id + "F58", { "sketchPlane" : qUnion([Q0])});
            skLineSegment(sketch, "E65.bottom", {"start": v(61.51, -57.77) * mm, "end": v(37.51, -57.77) * mm});
            skLineSegment(sketch, "E65.top", {"start": v(61.51, -54.77) * mm, "end": v(37.51, -54.77) * mm});
            skLineSegment(sketch, "E65.left", {"start": v(61.51, -57.77) * mm, "end": v(61.51, -54.77) * mm});
            skLineSegment(sketch, "E65.right", {"start": v(37.51, -57.77) * mm, "end": v(37.51, -54.77) * mm});
            skSolve(sketch);
        }
        {
            var Q0;
            Q0 = qSketchRegion(id + "F58", true);
            extrude(context, id + "F59", {"entities" : qUnion([Q0]), "operationType" : NewBodyOperationType.REMOVE, "oppositeDirection" : true, "depth" : 12 * mm});
        }
        {
            var Q0;
            Q0=makeQuery(id+"F54.opExtrude","CAP_FACE",FACE,{"disambiguationData":[OSD([sQuery(id+"F53.wireOp",EDGE,"E63.bottom"),sQuery(id+"F53.wireOp",EDGE,"E63.top"),sQuery(id+"F53.wireOp",EDGE,"E63.left"),sQuery(id+"F53.wireOp",EDGE,"E63.right")])],"isStart":false});
            var sketch = newSketch(context, id + "F60", { "sketchPlane" : qUnion([Q0])});
            skLineSegment(sketch, "E66.bottom", {"start": v(-39.38, -57.77) * mm, "end": v(-61.38, -57.77) * mm});
            skLineSegment(sketch, "E66.top", {"start": v(-39.38, -54.77) * mm, "end": v(-61.38, -54.77) * mm});
            skLineSegment(sketch, "E66.left", {"start": v(-39.38, -57.77) * mm, "end": v(-39.38, -54.77) * mm});
            skLineSegment(sketch, "E66.right", {"start": v(-61.38, -57.77) * mm, "end": v(-61.38, -54.77) * mm});
            skSolve(sketch);
        }
        {
            var Q0;
            Q0 = qSketchRegion(id + "F60", true);
            extrude(context, id + "F61", {"entities" : qUnion([Q0]), "operationType" : NewBodyOperationType.REMOVE, "oppositeDirection" : true, "depth" : 12 * mm});
        }
        {
            var Q0;
            Q0=makeQuery(id+"F59.boolean.opBoolean","COPY",EDGE,{"derivedFrom":makeQuery(id+"F59.opExtrude","CAP_EDGE",EDGE,{"disambiguationData":[OSD([sQuery(id+"F58.wireOp",EDGE,"E65.right")])],"isStart":true})});
            var Q1;
            Q1=makeQuery(id+"F59.boolean.opBoolean","COPY",EDGE,{"derivedFrom":makeQuery(id+"F59.opExtrude","CAP_EDGE",EDGE,{"disambiguationData":[OSD([sQuery(id+"F58.wireOp",EDGE,"E65.left")])],"isStart":true})});
            var Q2;
            Q2=makeQuery(id+"F54.opExtrude","CAP_EDGE",EDGE,{"disambiguationData":[OSD([sQuery(id+"F53.wireOp",EDGE,"E62.right")])],"isStart":false});
            var Q3;
            Q3=makeQuery(id+"F54.opExtrude","CAP_EDGE",EDGE,{"disambiguationData":[OSD([sQuery(id+"F53.wireOp",EDGE,"E63.right")])],"isStart":false});
            var Q4;
            Q4=makeQuery(id+"F61.boolean.opBoolean","COPY",EDGE,{"derivedFrom":makeQuery(id+"F61.opExtrude","CAP_EDGE",EDGE,{"disambiguationData":[OSD([sQuery(id+"F60.wireOp",EDGE,"E66.left")])],"isStart":true})});
            var Q5;
            Q5=makeQuery(id+"F61.boolean.opBoolean","COPY",EDGE,{"derivedFrom":makeQuery(id+"F61.opExtrude","CAP_EDGE",EDGE,{"disambiguationData":[OSD([sQuery(id+"F60.wireOp",EDGE,"E66.right")])],"isStart":true})});
            fillet(context, id + "F62", {"entities" : qUnion([Q0, Q1, Q2, Q3, Q4, Q5]), "radius" : 1 * mm, "tangentPropagation" : true, "allowEdgeOverflow" : false});
        }
        {
            var Q0;
            Q0=makeQuery(id+"F2.opShell","OFFSET_FACE",FACE,{"disambiguationData":[OSD([sQuery(id+"F0.wireOp",EDGE,"E0.top"),sQuery(id+"F0.wireOp",EDGE,"E0.left"),sQuery(id+"F0.wireOp",EDGE,"E0.right"),sQuery(id+"F0.wireOp",EDGE,"E1"),sQuery(id+"F0.wireOp",EDGE,"E2"),sQuery(id+"F0.wireOp",EDGE,"E3"),sQuery(id+"F0.wireOp",EDGE,"E4.filletArc"),sQuery(id+"F0.wireOp",EDGE,"E5.filletArc"),sQuery(id+"F0.wireOp",EDGE,"E6.filletArc"),sQuery(id+"F0.wireOp",EDGE,"E7.filletArc"),sQuery(id+"F0.wireOp",EDGE,"E8.filletArc"),sQuery(id+"F0.wireOp",EDGE,"E9.filletArc")])]});
            var sketch = newSketch(context, id + "F63", { "sketchPlane" : qUnion([Q0])});
            skLineSegment(sketch, "E67.bottom", {"start": v(-25.15, -38.16) * mm, "end": v(1.85, -38.16) * mm});
            skLineSegment(sketch, "E67.top", {"start": v(-25.15, 31.84) * mm, "end": v(1.85, 31.84) * mm});
            skLineSegment(sketch, "E67.left", {"start": v(-25.15, -38.16) * mm, "end": v(-25.15, 31.84) * mm});
            skLineSegment(sketch, "E67.right", {"start": v(1.85, -38.16) * mm, "end": v(1.85, 31.84) * mm});
            skSolve(sketch);
        }
        {
            var Q0;
            Q0 = qSketchRegion(id + "F63", true);
            extrude(context, id + "F64", {"entities" : qUnion([Q0]), "operationType" : NewBodyOperationType.ADD, "depth" : 5 * mm});
        }
        {
            var Q0;
            Q0=makeQuery(id+"F64.opExtrude","CAP_EDGE",EDGE,{"disambiguationData":[OSD([sQuery(id+"F63.wireOp",EDGE,"E67.bottom")])],"isStart":false});
            var Q1;
            Q1=makeQuery(id+"F64.opExtrude","CAP_EDGE",EDGE,{"disambiguationData":[OSD([sQuery(id+"F63.wireOp",EDGE,"E67.right")])],"isStart":false});
            var Q2;
            Q2=makeQuery(id+"F64.opExtrude","CAP_EDGE",EDGE,{"disambiguationData":[OSD([sQuery(id+"F63.wireOp",EDGE,"E67.top")])],"isStart":false});
            var Q3;
            {var subQ0=sQuery(id+"F63.wireOp",EDGE,"E67.left");Q3=makeQuery(id+"F64.boolean.opBoolean","SPLIT",EDGE,{"disambiguationData":[topologyDisambiguationEdgeConnected([makeQuery(id+"F64.opExtrude","SWEPT_FACE",FACE,{"disambiguationData":[OSD([subQ0])]})])],"derivedFrom":makeQuery(id+"F64.opExtrude","CAP_EDGE",EDGE,{"disambiguationData":[OSD([subQ0])],"isStart":false})});}
            fillet(context, id + "F65", {"entities" : qUnion([Q0, Q1, Q2, Q3]), "radius" : 1 * mm, "tangentPropagation" : true, "allowEdgeOverflow" : false});
        }
        {
            var Q0;
            Q0=makeQuery(id+"F1.opExtrude","CAP_FACE",FACE,{"disambiguationData":[OSD([sQuery(id+"F0.wireOp",EDGE,"E0.top"),sQuery(id+"F0.wireOp",EDGE,"E0.left"),sQuery(id+"F0.wireOp",EDGE,"E0.right"),sQuery(id+"F0.wireOp",EDGE,"E1"),sQuery(id+"F0.wireOp",EDGE,"E2"),sQuery(id+"F0.wireOp",EDGE,"E3"),sQuery(id+"F0.wireOp",EDGE,"E4.filletArc"),sQuery(id+"F0.wireOp",EDGE,"E5.filletArc"),sQuery(id+"F0.wireOp",EDGE,"E6.filletArc"),sQuery(id+"F0.wireOp",EDGE,"E7.filletArc"),sQuery(id+"F0.wireOp",EDGE,"E8.filletArc"),sQuery(id+"F0.wireOp",EDGE,"E9.filletArc")])],"isStart":true});
            var sketch = newSketch(context, id + "F66", { "sketchPlane" : qUnion([Q0])});
            skLineSegment(sketch, "E68.bottom", {"start": v(20.05, -62.47) * mm, "end": v(28.85, -62.47) * mm});
            skLineSegment(sketch, "E68.top", {"start": v(20.05, -59.47) * mm, "end": v(28.85, -59.47) * mm});
            skLineSegment(sketch, "E68.left", {"start": v(20.05, -62.47) * mm, "end": v(20.05, -59.47) * mm});
            skLineSegment(sketch, "E68.right", {"start": v(28.85, -62.47) * mm, "end": v(28.85, -59.47) * mm});
            skSolve(sketch);
        }
        {
            var Q0;
            Q0 = qSketchRegion(id + "F66", true);
            extrude(context, id + "F67", {"entities" : qUnion([Q0]), "operationType" : NewBodyOperationType.REMOVE, "oppositeDirection" : true, "depth" : 5 * mm, "offsetDistance" : 25 * mm});
        }
        {
            var Q0;
            Q0=makeQuery(id+"F67.boolean.opBoolean","INTERSECT",EDGE,{"derivedFrom":[makeQuery(id+"F2.opShell","OFFSET_FACE",FACE,{"disambiguationData":[OSD([sQuery(id+"F0.wireOp",EDGE,"E0.top"),sQuery(id+"F0.wireOp",EDGE,"E0.left"),sQuery(id+"F0.wireOp",EDGE,"E0.right"),sQuery(id+"F0.wireOp",EDGE,"E1"),sQuery(id+"F0.wireOp",EDGE,"E2"),sQuery(id+"F0.wireOp",EDGE,"E3"),sQuery(id+"F0.wireOp",EDGE,"E4.filletArc"),sQuery(id+"F0.wireOp",EDGE,"E5.filletArc"),sQuery(id+"F0.wireOp",EDGE,"E6.filletArc"),sQuery(id+"F0.wireOp",EDGE,"E7.filletArc"),sQuery(id+"F0.wireOp",EDGE,"E8.filletArc"),sQuery(id+"F0.wireOp",EDGE,"E9.filletArc")])]}),makeQuery(id+"F67.opExtrude","SWEPT_FACE",FACE,{"disambiguationData":[OSD([sQuery(id+"F66.wireOp",EDGE,"E68.top")])]})]});
            var Q1;
            Q1=makeQuery(id+"F67.boolean.opBoolean","INTERSECT",EDGE,{"derivedFrom":[makeQuery(id+"F2.opShell","OFFSET_FACE",FACE,{"disambiguationData":[OSD([sQuery(id+"F0.wireOp",EDGE,"E0.top"),sQuery(id+"F0.wireOp",EDGE,"E0.left"),sQuery(id+"F0.wireOp",EDGE,"E0.right"),sQuery(id+"F0.wireOp",EDGE,"E1"),sQuery(id+"F0.wireOp",EDGE,"E2"),sQuery(id+"F0.wireOp",EDGE,"E3"),sQuery(id+"F0.wireOp",EDGE,"E4.filletArc"),sQuery(id+"F0.wireOp",EDGE,"E5.filletArc"),sQuery(id+"F0.wireOp",EDGE,"E6.filletArc"),sQuery(id+"F0.wireOp",EDGE,"E7.filletArc"),sQuery(id+"F0.wireOp",EDGE,"E8.filletArc"),sQuery(id+"F0.wireOp",EDGE,"E9.filletArc")])]}),makeQuery(id+"F67.opExtrude","SWEPT_FACE",FACE,{"disambiguationData":[OSD([sQuery(id+"F66.wireOp",EDGE,"E68.left")])]})]});
            var Q2;
            Q2=makeQuery(id+"F67.boolean.opBoolean","INTERSECT",EDGE,{"derivedFrom":[makeQuery(id+"F2.opShell","OFFSET_FACE",FACE,{"disambiguationData":[OSD([sQuery(id+"F0.wireOp",EDGE,"E0.top"),sQuery(id+"F0.wireOp",EDGE,"E0.left"),sQuery(id+"F0.wireOp",EDGE,"E0.right"),sQuery(id+"F0.wireOp",EDGE,"E1"),sQuery(id+"F0.wireOp",EDGE,"E2"),sQuery(id+"F0.wireOp",EDGE,"E3"),sQuery(id+"F0.wireOp",EDGE,"E4.filletArc"),sQuery(id+"F0.wireOp",EDGE,"E5.filletArc"),sQuery(id+"F0.wireOp",EDGE,"E6.filletArc"),sQuery(id+"F0.wireOp",EDGE,"E7.filletArc"),sQuery(id+"F0.wireOp",EDGE,"E8.filletArc"),sQuery(id+"F0.wireOp",EDGE,"E9.filletArc")])]}),makeQuery(id+"F67.opExtrude","SWEPT_FACE",FACE,{"disambiguationData":[OSD([sQuery(id+"F66.wireOp",EDGE,"E68.bottom")])]})]});
            var Q3;
            Q3=makeQuery(id+"F67.boolean.opBoolean","INTERSECT",EDGE,{"derivedFrom":[makeQuery(id+"F2.opShell","OFFSET_FACE",FACE,{"disambiguationData":[OSD([sQuery(id+"F0.wireOp",EDGE,"E0.top"),sQuery(id+"F0.wireOp",EDGE,"E0.left"),sQuery(id+"F0.wireOp",EDGE,"E0.right"),sQuery(id+"F0.wireOp",EDGE,"E1"),sQuery(id+"F0.wireOp",EDGE,"E2"),sQuery(id+"F0.wireOp",EDGE,"E3"),sQuery(id+"F0.wireOp",EDGE,"E4.filletArc"),sQuery(id+"F0.wireOp",EDGE,"E5.filletArc"),sQuery(id+"F0.wireOp",EDGE,"E6.filletArc"),sQuery(id+"F0.wireOp",EDGE,"E7.filletArc"),sQuery(id+"F0.wireOp",EDGE,"E8.filletArc"),sQuery(id+"F0.wireOp",EDGE,"E9.filletArc")])]}),makeQuery(id+"F67.opExtrude","SWEPT_FACE",FACE,{"disambiguationData":[OSD([sQuery(id+"F66.wireOp",EDGE,"E68.right")])]})]});
            var Q4;
            Q4=makeQuery(id+"F67.boolean.opBoolean","COPY",EDGE,{"derivedFrom":makeQuery(id+"F67.opExtrude","CAP_EDGE",EDGE,{"disambiguationData":[OSD([sQuery(id+"F66.wireOp",EDGE,"E68.right")])],"isStart":true})});
            var Q5;
            Q5=makeQuery(id+"F67.boolean.opBoolean","COPY",EDGE,{"derivedFrom":makeQuery(id+"F67.opExtrude","CAP_EDGE",EDGE,{"disambiguationData":[OSD([sQuery(id+"F66.wireOp",EDGE,"E68.bottom")])],"isStart":true})});
            var Q6;
            Q6=makeQuery(id+"F67.boolean.opBoolean","COPY",EDGE,{"derivedFrom":makeQuery(id+"F67.opExtrude","CAP_EDGE",EDGE,{"disambiguationData":[OSD([sQuery(id+"F66.wireOp",EDGE,"E68.left")])],"isStart":true})});
            var Q7;
            Q7=makeQuery(id+"F67.boolean.opBoolean","COPY",EDGE,{"derivedFrom":makeQuery(id+"F67.opExtrude","CAP_EDGE",EDGE,{"disambiguationData":[OSD([sQuery(id+"F66.wireOp",EDGE,"E68.top")])],"isStart":true})});
            var Q8;
            Q8=makeQuery(id+"F67.boolean.opBoolean","INTERSECT",EDGE,{"derivedFrom":[makeQuery(id+"F2.opShell","OFFSET_FACE",FACE,{"disambiguationData":[OSD([sQuery(id+"F0.wireOp",EDGE,"E0.top"),sQuery(id+"F0.wireOp",EDGE,"E0.left"),sQuery(id+"F0.wireOp",EDGE,"E0.right"),sQuery(id+"F0.wireOp",EDGE,"E1"),sQuery(id+"F0.wireOp",EDGE,"E2"),sQuery(id+"F0.wireOp",EDGE,"E3"),sQuery(id+"F0.wireOp",EDGE,"E4.filletArc"),sQuery(id+"F0.wireOp",EDGE,"E5.filletArc"),sQuery(id+"F0.wireOp",EDGE,"E6.filletArc"),sQuery(id+"F0.wireOp",EDGE,"E7.filletArc"),sQuery(id+"F0.wireOp",EDGE,"E8.filletArc"),sQuery(id+"F0.wireOp",EDGE,"E9.filletArc")])]}),makeQuery(id+"F67.opExtrude","SWEPT_FACE",FACE,{"disambiguationData":[OSD([sQuery(id+"F66.wireOp",EDGE,"V19e69mw-SfjY-St0u-Nz9I-2bYdwGw74nQ4.bottom")])]})]});
            var Q9;
            Q9=makeQuery(id+"F67.boolean.opBoolean","INTERSECT",EDGE,{"derivedFrom":[makeQuery(id+"F2.opShell","OFFSET_FACE",FACE,{"disambiguationData":[OSD([sQuery(id+"F0.wireOp",EDGE,"E0.top"),sQuery(id+"F0.wireOp",EDGE,"E0.left"),sQuery(id+"F0.wireOp",EDGE,"E0.right"),sQuery(id+"F0.wireOp",EDGE,"E1"),sQuery(id+"F0.wireOp",EDGE,"E2"),sQuery(id+"F0.wireOp",EDGE,"E3"),sQuery(id+"F0.wireOp",EDGE,"E4.filletArc"),sQuery(id+"F0.wireOp",EDGE,"E5.filletArc"),sQuery(id+"F0.wireOp",EDGE,"E6.filletArc"),sQuery(id+"F0.wireOp",EDGE,"E7.filletArc"),sQuery(id+"F0.wireOp",EDGE,"E8.filletArc"),sQuery(id+"F0.wireOp",EDGE,"E9.filletArc")])]}),makeQuery(id+"F67.opExtrude","SWEPT_FACE",FACE,{"disambiguationData":[OSD([sQuery(id+"F66.wireOp",EDGE,"V19e69mw-SfjY-St0u-Nz9I-2bYdwGw74nQ4.left")])]})]});
            var Q10;
            Q10=makeQuery(id+"F67.boolean.opBoolean","INTERSECT",EDGE,{"derivedFrom":[makeQuery(id+"F2.opShell","OFFSET_FACE",FACE,{"disambiguationData":[OSD([sQuery(id+"F0.wireOp",EDGE,"E0.top"),sQuery(id+"F0.wireOp",EDGE,"E0.left"),sQuery(id+"F0.wireOp",EDGE,"E0.right"),sQuery(id+"F0.wireOp",EDGE,"E1"),sQuery(id+"F0.wireOp",EDGE,"E2"),sQuery(id+"F0.wireOp",EDGE,"E3"),sQuery(id+"F0.wireOp",EDGE,"E4.filletArc"),sQuery(id+"F0.wireOp",EDGE,"E5.filletArc"),sQuery(id+"F0.wireOp",EDGE,"E6.filletArc"),sQuery(id+"F0.wireOp",EDGE,"E7.filletArc"),sQuery(id+"F0.wireOp",EDGE,"E8.filletArc"),sQuery(id+"F0.wireOp",EDGE,"E9.filletArc")])]}),makeQuery(id+"F67.opExtrude","SWEPT_FACE",FACE,{"disambiguationData":[OSD([sQuery(id+"F66.wireOp",EDGE,"V19e69mw-SfjY-St0u-Nz9I-2bYdwGw74nQ4.right")])]})]});
            var Q11;
            Q11=makeQuery(id+"F67.boolean.opBoolean","INTERSECT",EDGE,{"derivedFrom":[makeQuery(id+"F2.opShell","OFFSET_FACE",FACE,{"disambiguationData":[OSD([sQuery(id+"F0.wireOp",EDGE,"E0.top"),sQuery(id+"F0.wireOp",EDGE,"E0.left"),sQuery(id+"F0.wireOp",EDGE,"E0.right"),sQuery(id+"F0.wireOp",EDGE,"E1"),sQuery(id+"F0.wireOp",EDGE,"E2"),sQuery(id+"F0.wireOp",EDGE,"E3"),sQuery(id+"F0.wireOp",EDGE,"E4.filletArc"),sQuery(id+"F0.wireOp",EDGE,"E5.filletArc"),sQuery(id+"F0.wireOp",EDGE,"E6.filletArc"),sQuery(id+"F0.wireOp",EDGE,"E7.filletArc"),sQuery(id+"F0.wireOp",EDGE,"E8.filletArc"),sQuery(id+"F0.wireOp",EDGE,"E9.filletArc")])]}),makeQuery(id+"F67.opExtrude","SWEPT_FACE",FACE,{"disambiguationData":[OSD([sQuery(id+"F66.wireOp",EDGE,"V19e69mw-SfjY-St0u-Nz9I-2bYdwGw74nQ4.top")])]})]});
            var Q12;
            Q12=makeQuery(id+"F67.boolean.opBoolean","COPY",EDGE,{"derivedFrom":makeQuery(id+"F67.opExtrude","CAP_EDGE",EDGE,{"disambiguationData":[OSD([sQuery(id+"F66.wireOp",EDGE,"V19e69mw-SfjY-St0u-Nz9I-2bYdwGw74nQ4.bottom")])],"isStart":true})});
            var Q13;
            Q13=makeQuery(id+"F67.boolean.opBoolean","COPY",EDGE,{"derivedFrom":makeQuery(id+"F67.opExtrude","CAP_EDGE",EDGE,{"disambiguationData":[OSD([sQuery(id+"F66.wireOp",EDGE,"V19e69mw-SfjY-St0u-Nz9I-2bYdwGw74nQ4.right")])],"isStart":true})});
            var Q14;
            Q14=makeQuery(id+"F67.boolean.opBoolean","COPY",EDGE,{"derivedFrom":makeQuery(id+"F67.opExtrude","CAP_EDGE",EDGE,{"disambiguationData":[OSD([sQuery(id+"F66.wireOp",EDGE,"V19e69mw-SfjY-St0u-Nz9I-2bYdwGw74nQ4.left")])],"isStart":true})});
            var Q15;
            Q15=makeQuery(id+"F67.boolean.opBoolean","COPY",EDGE,{"derivedFrom":makeQuery(id+"F67.opExtrude","CAP_EDGE",EDGE,{"disambiguationData":[OSD([sQuery(id+"F66.wireOp",EDGE,"V19e69mw-SfjY-St0u-Nz9I-2bYdwGw74nQ4.top")])],"isStart":true})});
            fillet(context, id + "F68", {"entities" : qUnion([Q0, Q1, Q2, Q3, Q4, Q5, Q6, Q7, Q8, Q9, Q10, Q11, Q12, Q13, Q14, Q15]), "radius" : 0.7 * mm, "tangentPropagation" : true, "allowEdgeOverflow" : false});
        }
    });
